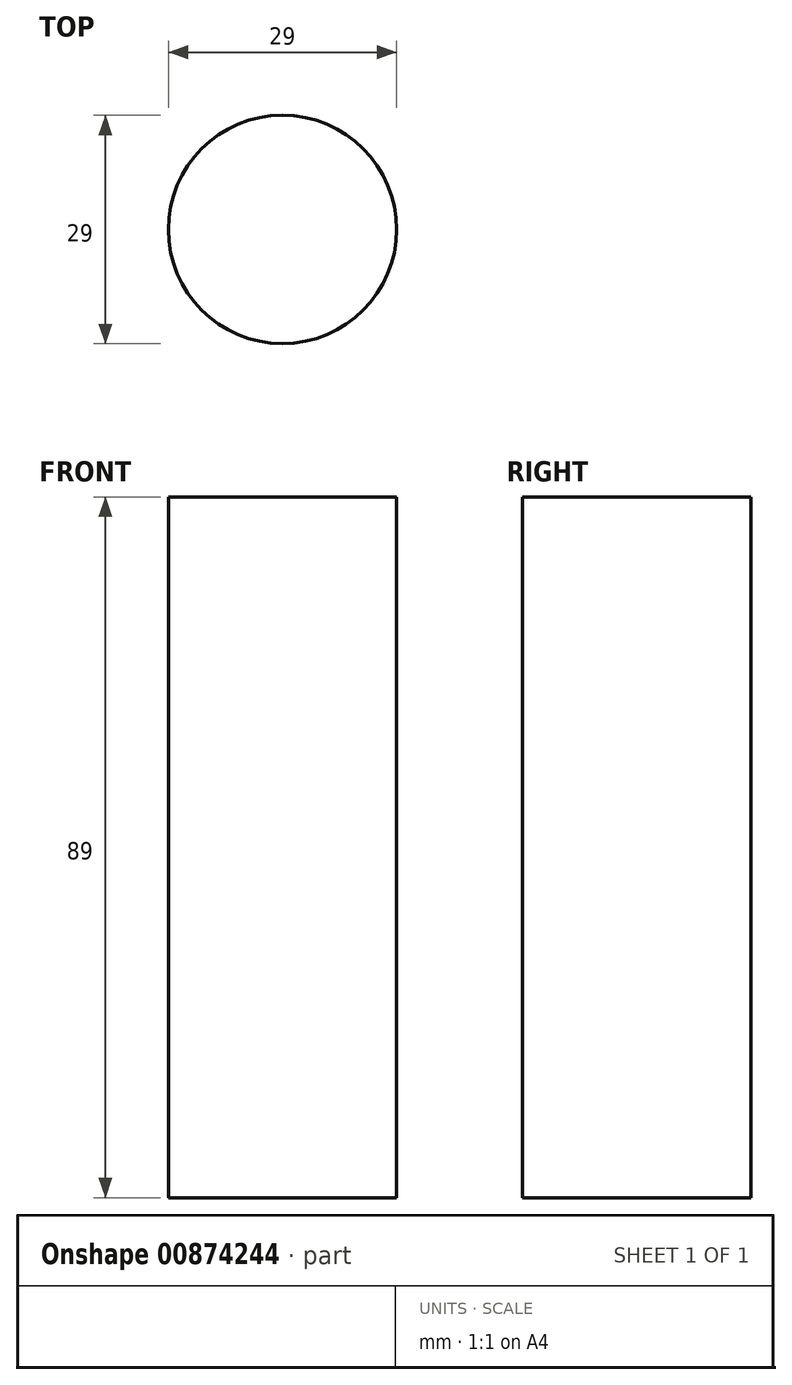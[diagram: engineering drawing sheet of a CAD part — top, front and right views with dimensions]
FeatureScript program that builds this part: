
annotation { "Feature Type Name" : "Feature", "Feature Type Description" : "" }
export const myFeature = defineFeature(function(context is Context, id is Id, definition is map)
    precondition{}
    {
        {
            var Q0;
            Q0=qCreatedBy(makeId("Top.planeOp"),FACE);
            var sketch = newSketch(context, id + "F0", { "sketchPlane" : qUnion([Q0])});
            skCircle(sketch, "E0", {"center": v(0, 0) * mm, "radius": 14.5 * mm});
            skSolve(sketch);
        }
        {
            var Q0;
            Q0 = qSketchRegion(id + "F0", true);
            extrude(context, id + "F1", {"entities" : qUnion([Q0]), "depth" : 89 * mm, "offsetDistance" : 25.4 * mm});
        }
    });
